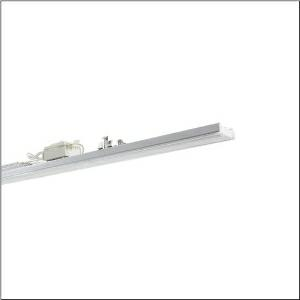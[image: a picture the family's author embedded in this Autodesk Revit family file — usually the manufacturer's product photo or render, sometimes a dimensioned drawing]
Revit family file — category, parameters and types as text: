
# Revit family: licross_11_recessed_mo_51tl12dn4axg
name_source: partatom
category: Lighting Fixtures
units: mm (PartAtom-declared; Revit-internal decimal feet)

## family parameters
Cut with Voids When Loaded = No
Host = Face
Light Source = No
Part Type = Normal
Room Calculation Point = No
Round Connector Dimension = Use Diameter
Shared = No

## types (1)
- --- (1 x LED, 10240 lm, 56.7 W, 4000K)
    Apparent Load = 57 VA
    CIE Flux Codes = 67 92 99 100 100
    Color Rendering = 80
    Color Temperature = 4000K
    Default Elevation = 1800 mm
    Description = Licross 11 Recessed MO, luminaire insert, of sheet steel, coil coated, white, length: 1.500mm, width: 66mm, height: 67mm, LED rated luminous flux: 10.240lm, light colour: 840, SDCM (Standard Deviation of Colour Matching)MacAdam ≤ 2 SDCM (initial), control gear: DALI 2, with plug, 5-pole, with phase selection, mains connection: 220..240V, AC, 50/60Hz, rated input power: 57W, internal wiring halogen-free, primary optical cover: cover, of PMMA, light emission: direct distribution, primary light characteristic: symmetric, protection rating (complete): IP40, insulation class (complete): insulation class I (protective earthing), certification: CE, ENEC, VDE, UKCA, protection symbol: D if used in an environment without relevant dust loads with corresponding accessories, impact resistance: IK06, permissible ambient temperature for indoor applications: -25..+35°C, corresponds to IFS (International Featured Standards) requirements for safety and quality in the food industry, reducing of maximum allowable ambient temperature of 5°C with ceiling mounting, LABS conformity tested according to VDMA 24364:2018-05, The light source and the operating device comply with the requirements of the Ecodesign Regulation (EU) 2019/2020 and are replaceable in accordance with this regulation, packaging unit: 1 piece
    Height = 58 mm
    Lamp = 1 x LED
    Lamp Light Flux = 10240 lm
    Lamp Power = 56.7 W
    Lamp count = 1
    Length = 1500 mm
    Luminous efficacy = 181 lm/W
    Manufacturer = Siteco
    ModVariant = No
    Model = 51TL12DN4AXG
    Mounting Place = Ceiling
    Mounting Type = Pendant
    Number of Poles = 1
    OnlyDefault = Yes
    Power Factor = 1
    Product Name = Licross 11 Recessed MO
    Product group = luminaire insert | ceiling pendant
    ProductGroupID = 901
    Protection Class = Protection class I
    Protection Degree = IP 40
    RLX_Detail_Level = 1
    RLX_Emergency_Light_Flux = 0 lm
    RLX_Emergency_Type = 0
    RLX_Emergency_Type_DB = No
    RlxData = <blob elided: 24649 chars, md5=1d5dc44f>
    Socket = socket
    Standby Power = 0 W
    System Light Flux = 10240 lm
    System Power = 57 W
    Type Comments = factory setting: luminous flux: 100 % | dim-lin: 254 | 378 mA
    Type Image = l_1296930.jpg
    URL = http://relux.com
    VarID = @adj_101891
    Voltage = 0 V
    Weight = 0.00 kg
    Width = 66 mm

## geometry (parser evidence)
native form markers: Blend x4, Sweep x11
no freeform markers — native parametric forms only
